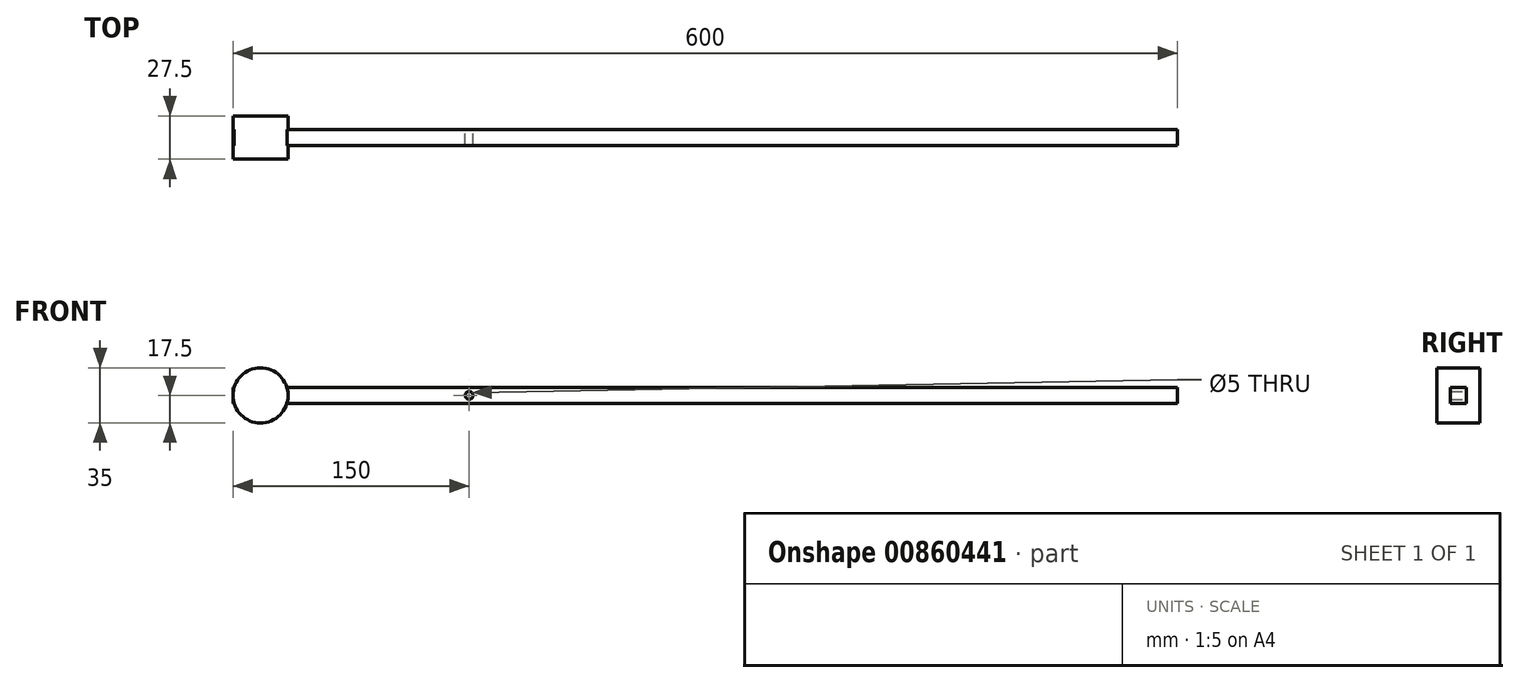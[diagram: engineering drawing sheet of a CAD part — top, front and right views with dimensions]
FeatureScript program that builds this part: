
annotation { "Feature Type Name" : "Feature", "Feature Type Description" : "" }
export const myFeature = defineFeature(function(context is Context, id is Id, definition is map)
    precondition{}
    {
        {
            var Q0;
            Q0=qCreatedBy(makeId("Front.planeOp"),FACE);
            var sketch = newSketch(context, id + "F0", { "sketchPlane" : qUnion([Q0])});
            skLineSegment(sketch, "E0.bottom", {"start": v(300, -5) * mm, "end": v(-300, -5) * mm});
            skLineSegment(sketch, "E0.top", {"start": v(300, 5) * mm, "end": v(-300, 5) * mm});
            skLineSegment(sketch, "E0.left", {"start": v(300, -5) * mm, "end": v(300, 5) * mm});
            skLineSegment(sketch, "E0.right", {"start": v(-300, -5) * mm, "end": v(-300, 5) * mm});
            skPoint(sketch, "E0.middle", {"position": v(0, 0) * mm});
            skLineSegment(sketch, "E1", {"start": v(-300, 0) * mm, "end": v(-150, 0) * mm});
            skCircle(sketch, "E2", {"center": v(-150, 0) * mm, "radius": 5 * mm});
            skCircle(sketch, "E3", {"center": v(-150, 0) * mm, "radius": 2.5 * mm});
            skSolve(sketch);
        }
        {
            var Q0;
            {var subQ0=sQuery(id+"F0.wireOp",EDGE,"E0.left");Q0=makeQuery(id+"F0.imprint","IMPRINT",FACE,{"disambiguationData":[TD([[makeQuery(id+"F0.imprint","IMPRINT",EDGE,{"derivedFrom":subQ0}),1.0]])]});}
            var Q1;
            {var subQ0=sQuery(id+"F0.wireOp",EDGE,"E0.right");var subQ1=sQuery(id+"F0.wireOp",EDGE,"E0.bottom");var subQ2=makeQuery(id+"F0.imprint","INTERSECT",VERTEX,{"derivedFrom":[subQ1,subQ0]});Q1=makeQuery(id+"F0.imprint","IMPRINT",FACE,{"disambiguationData":[TD([[makeQuery(id+"F0.imprint","IMPRINT",EDGE,{"disambiguationData":[TD([[subQ2,1.0]])],"derivedFrom":subQ1}),-1.0]])]});}
            var Q2;
            {var subQ0=sQuery(id+"F0.wireOp",EDGE,"E0.right");var subQ1=sQuery(id+"F0.wireOp",EDGE,"E0.top");var subQ2=makeQuery(id+"F0.imprint","INTERSECT",VERTEX,{"derivedFrom":[subQ1,subQ0]});Q2=makeQuery(id+"F0.imprint","IMPRINT",FACE,{"disambiguationData":[TD([[makeQuery(id+"F0.imprint","IMPRINT",EDGE,{"disambiguationData":[TD([[subQ2,1.0]])],"derivedFrom":subQ1}),1.0]])]});}
            var Q3;
            Q3=makeQuery(id+"F0.imprint","IMPRINT",FACE,{"disambiguationData":[TD([[makeQuery(id+"F0.imprint","IMPRINT",EDGE,{"derivedFrom":sQuery(id+"F0.wireOp",EDGE,"E3")}),-1.0]])]});
            extrude(context, id + "F1", {"entities" : qUnion([Q0, Q1, Q2, Q3]), "depth" : 10 * mm, "offsetDistance" : 25 * mm});
        }
        {
            var Q0;
            Q0=makeQuery(id+"F1.opExtrude","CAP_FACE",FACE,{"disambiguationData":[OSD([sQuery(id+"F0.wireOp",EDGE,"E0.bottom"),sQuery(id+"F0.wireOp",EDGE,"E0.top"),sQuery(id+"F0.wireOp",EDGE,"E0.left"),sQuery(id+"F0.wireOp",EDGE,"E0.right"),sQuery(id+"F0.wireOp",EDGE,"E3")])],"isStart":false});
            var sketch = newSketch(context, id + "F2", { "sketchPlane" : qUnion([Q0])});
            skLineSegment(sketch, "E4", {"start": v(-300, 0) * mm, "end": v(-282.5, 0) * mm});
            skCircle(sketch, "E5", {"center": v(-282.5, 0) * mm, "radius": 17.5 * mm});
            skSolve(sketch);
        }
        {
            var Q0;
            Q0 = qSketchRegion(id + "F2", true);
            extrude(context, id + "F3", {"entities" : qUnion([Q0]), "operationType" : NewBodyOperationType.ADD, "depth" : 8.75 * mm, "offsetDistance" : 25 * mm, "hasSecondDirection" : true, "secondDirectionOppositeDirection" : true, "secondDirectionDepth" : 18.75 * mm});
        }
    });
